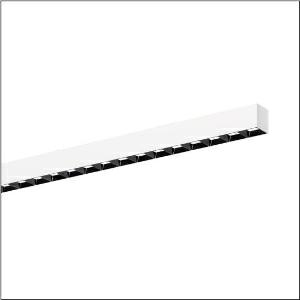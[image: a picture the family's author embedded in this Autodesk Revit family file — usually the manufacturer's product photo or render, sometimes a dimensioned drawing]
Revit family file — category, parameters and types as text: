
# Revit family: silica_r__21_51mx21dc4awb_19b2
name_source: partatom
category: Lighting Fixtures
units: mm (PartAtom-declared; Revit-internal decimal feet)

## family parameters
Cut with Voids When Loaded = No
Host = Face
Light Source = No
Part Type = Normal
Room Calculation Point = No
Round Connector Dimension = Use Diameter
Shared = No

## types (1)
- --- (1 x LED, 10800 lm, 64.8 W, 4000K)
    Apparent Load = 65 VA
    CIE Flux Codes = 87 99 100 100 100
    Color Rendering = 80
    Color Temperature = 4000K
    Default Elevation = 1800 mm
    Description = Silica® 21, office luminaire, primary light control with darklight reflector, of PMMA, black, CAT 2 (L<= 3000cd/m²), light emission: direct distribution, primary light characteristic: symmetric, installation type: surface-mounted, LED, rated luminous flux: 10.800lm, luminous efficacy: 167lm/W, light colour: 840, colour temperature: 4000K, with terminal, 3+2-pole, max. 2.5mm², mains connection: 220..240V, AC, 50/60Hz, rated input power: 64.8W, luminaire housing, of aluminium, traffic white (RAL 9016), length: 3.004mm, width: 53mm, height: 53mm, protection rating (complete): IP20, insulation class (complete): insulation class I (protective earthing), certification: CE, permissible operating ambient temperature: 0..+35°C, standard: EN 50419, packaging unit: 1 piece
    Height = 0 mm  [stored 0 ft]
    Lamp = 1 x LED
    Lamp Light Flux = 10800 lm
    Lamp Power = 64.8 W
    Lamp count = 1
    Length = 3004 mm
    Luminous efficacy = 167 lm/W
    Manufacturer = Siteco
    ModVariant = No
    Model = 51MX21DC4AWB
    Mounting Place = Ceiling
    Mounting Type = Recessed
    Number of Poles = 1
    OnlyDefault = Yes
    Power Factor = 1
    Product Name = Silica® 21
    Product group = office luminaire | ceiling recessed
    ProductGroupID = 400
    Protection Class = Protection class I
    Protection Degree = IP 20
    RLX_Detail_Level = 1
    RLX_Emergency_Light_Flux = 0 lm
    RLX_Emergency_Type = 0
    RLX_Emergency_Type_DB = No
    RlxData = <blob elided: 63073 chars, md5=27d50e83>
    Socket = socket
    Standby Power = 0 W
    System Light Flux = 10800 lm
    System Power = 65 W
    Type Comments = factory setting: luminous flux: 100 % | dim-lin: 254 | 367 mA
    Type Image = l_1335873.jpg
    URL = http://relux.com
    VarID = @adj_093629
    Voltage = 0 V
    Weight = 0.00 kg
    Width = 53 mm

note: [stored X ft] marks values corroborated as IEEE doubles in the binary element streams (Revit-internal decimal feet)

## geometry (parser evidence)
native form markers: Blend x4, Sweep x9
no freeform markers — native parametric forms only
